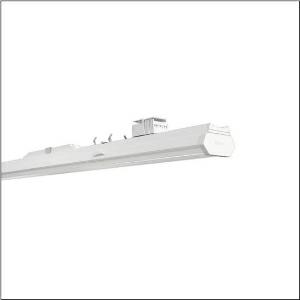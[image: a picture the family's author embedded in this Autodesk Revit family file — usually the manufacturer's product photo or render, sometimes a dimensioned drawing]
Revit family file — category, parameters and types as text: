
# Revit family: licross_r__11_protected_ho_51tp12dn4exl_09de
name_source: partatom
category: Lighting Fixtures
units: mm (PartAtom-declared; Revit-internal decimal feet)

## family parameters
Cut with Voids When Loaded = No
Host = Face
Light Source = No
Part Type = Normal
Room Calculation Point = No
Round Connector Dimension = Use Diameter
Shared = No

## types (1)
- --- (1 x LED, 14070 lm, 86.1 W, 4000K)
    Apparent Load = 86 VA
    CIE Flux Codes = 70 91 97 98 100
    Color Rendering = 80
    Color Temperature = 4000K
    Default Elevation = 1800 mm
    Description = Licross® 11 Protected HOluminaire insert, length: 1.500mm, width: 90mm, height: 101mm, LED rated luminous flux: 14.070lm, light colour: 840, control gear: DALI 2, control gear: ECG DALI, with plug, 5-pole, with phase selection, mains connection: 220..240V, AC, 50/60Hz, halogen-free wiring, primary optical cover: cover, of PMMA, light emission: direct with ceiling illumination distribution, protection rating (complete): IP64, insulation class (complete): insulation class I (protective earthing), certification: CE, ENEC, VDE, protection symbol: D if used in an environment with conductive dust loads with corresponding accessories, permissible ambient temperature for indoor applications: -25..+35°C, reducing of maximum allowable ambient temperature of 5°C with ceiling mounting, corresponds to IFS (International Featured Standards) requirements for safety and quality in the food industry, packaging unit: 1 piece
    Height = 92 mm
    Lamp = 1 x LED
    Lamp Light Flux = 14070 lm
    Lamp Power = 86.1 W
    Lamp count = 1
    Length = 1500 mm
    Luminous efficacy = 163 lm/W
    Manufacturer = Siteco
    ModVariant = No
    Model = 51TP12DN4EXL
    Mounting Place = Ceiling
    Mounting Type = Pendant
    Number of Poles = 1
    OnlyDefault = Yes
    Power Factor = 1
    Product Name = Licross® 11 Protected HO
    Product group = luminaire insert
    ProductGroupID = 902
    Protection Class = Protection class I
    Protection Degree = IP 64
    RLX_Detail_Level = 1
    RlxData = <blob elided: 24081 chars, md5=1a15b005>
    Socket = socket
    Standby Power = 0 W
    System Light Flux = 14070 lm
    System Power = 86 W
    Type Comments = factory setting: luminous flux: 100 % | dim-lin: 254 | 485 mA
    Type Image = l_1256148.jpg
    URL = http://relux.com
    VarID = @adj_138009
    Voltage = 0 V
    Weight = 0.00 kg
    Width = 88 mm

## geometry (parser evidence)
native form markers: Blend x4, Sweep x10
no freeform markers — native parametric forms only
